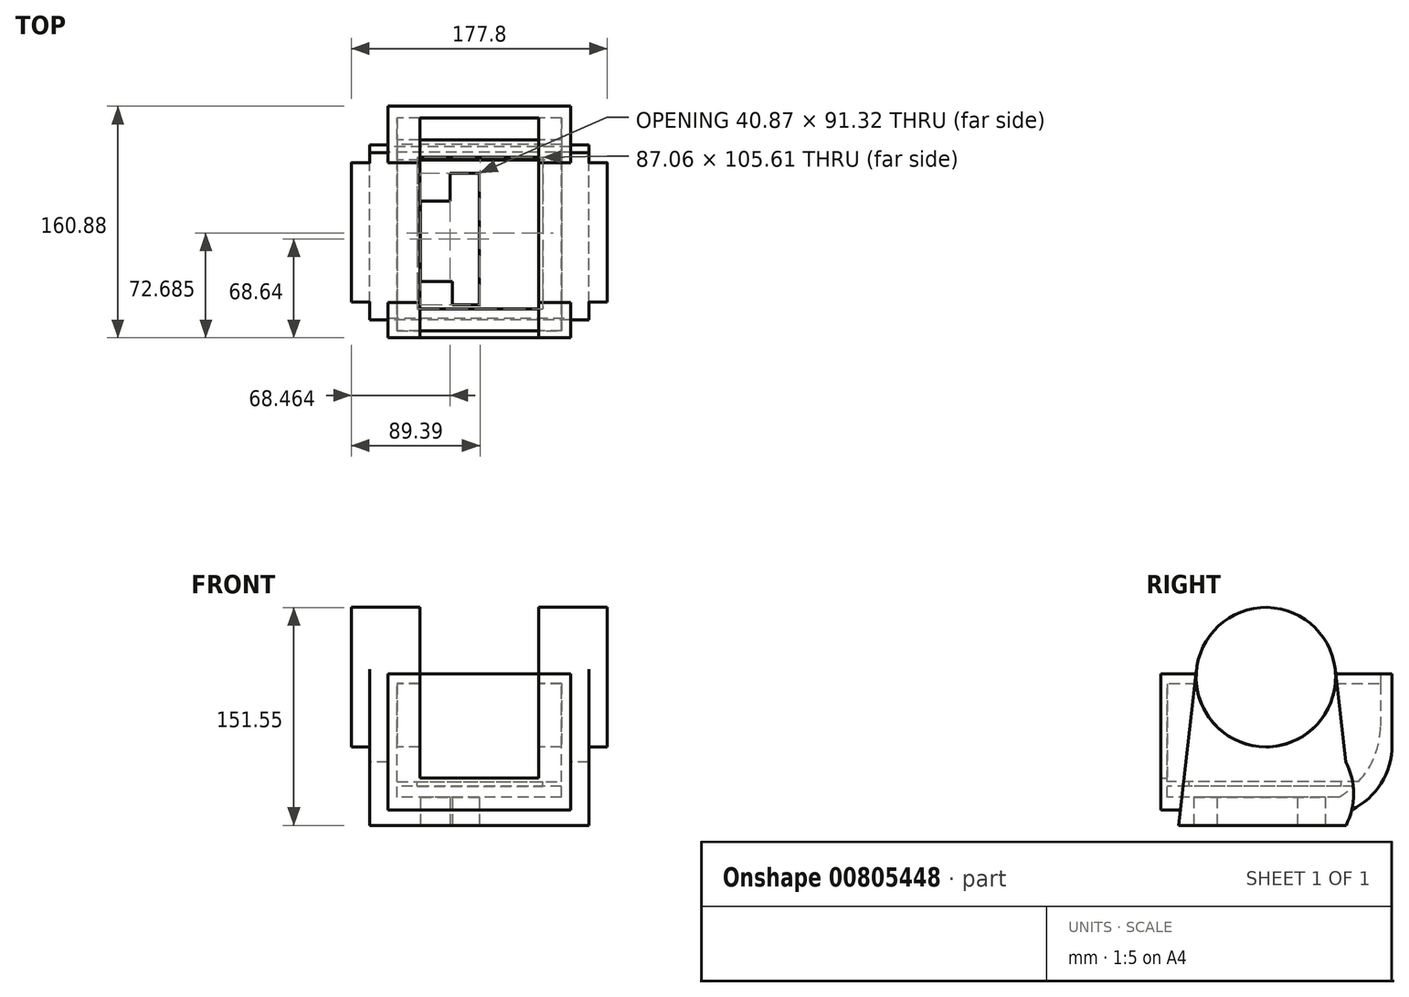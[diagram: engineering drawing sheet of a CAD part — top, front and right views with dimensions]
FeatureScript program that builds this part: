
annotation { "Feature Type Name" : "Feature", "Feature Type Description" : "" }
export const myFeature = defineFeature(function(context is Context, id is Id, definition is map)
    precondition{}
    {
        {
            var Q0;
            Q0=qCreatedBy(makeId("Right.planeOp"),FACE);
            var sketch = newSketch(context, id + "F0", { "sketchPlane" : qUnion([Q0])});
            skLineSegment(sketch, "E0", {"start": v(-58.2, 0) * mm, "end": v(58.24, 0) * mm});
            skArc(sketch, "E1", {"start": v(58.24, 0) * mm, "mid": v(63.47, 22.12) * mm, "end": v(58.05, 44.2) * mm});
            skLineSegment(sketch, "E2", {"start": v(58.05, 44.2) * mm, "end": v(50.61, 108.64) * mm});
            skArc(sketch, "E3", {"start": v(50.61, 108.64) * mm, "mid": v(2.47, 151.55) * mm, "end": v(-45.67, 108.64) * mm});
            skLineSegment(sketch, "E4", {"start": v(-45.67, 108.64) * mm, "end": v(-58.2, 0) * mm});
            skLineSegment(sketch, "E5", {"start": v(-45.67, 108.64) * mm, "end": v(50.61, 108.64) * mm, "construction": true});
            skSolve(sketch);
        }
        {
            var Q0;
            Q0 = qSketchRegion(id + "F0", true);
            extrude(context, id + "F1", {"entities" : qUnion([Q0]), "endBound" : BoundingType.SYMMETRIC, "depth" : 152.4 * mm, "offsetDistance" : 25.4 * mm});
        }
        {
            var Q0;
            Q0=qCreatedBy(makeId("Right.planeOp"),FACE);
            var sketch = newSketch(context, id + "F2", { "sketchPlane" : qUnion([Q0])});
            skCircle(sketch, "E6", {"center": v(2.47, 103.1) * mm, "radius": 48.46 * mm});
            skSolve(sketch);
        }
        {
            var Q0;
            Q0 = qSketchRegion(id + "F2", true);
            extrude(context, id + "F3", {"entities" : qUnion([Q0]), "operationType" : NewBodyOperationType.ADD, "endBound" : BoundingType.SYMMETRIC, "depth" : 177.8 * mm, "offsetDistance" : 25.4 * mm});
        }
        {
            var Q0;
            Q0=qCreatedBy(makeId("Right.planeOp"),FACE);
            var sketch = newSketch(context, id + "F4", { "sketchPlane" : qUnion([Q0])});
            skLineSegment(sketch, "E7", {"start": v(-70.63, 105.4) * mm, "end": v(90.25, 105.4) * mm});
            skLineSegment(sketch, "E8", {"start": v(90.25, 105.4) * mm, "end": v(90.25, 55.79) * mm});
            skArc(sketch, "E9", {"start": v(62.2, 10.85) * mm, "mid": v(82.66, 29.3) * mm, "end": v(90.25, 55.79) * mm});
            skLineSegment(sketch, "E10", {"start": v(-70.63, 105.4) * mm, "end": v(-70.63, 10.85) * mm});
            skLineSegment(sketch, "E11", {"start": v(-70.63, 10.85) * mm, "end": v(62.2, 10.85) * mm});
            skSolve(sketch);
        }
        {
            var Q0;
            Q0=makeQuery(id+"F4.imprint","IMPRINT",FACE,{"disambiguationData":[TD([[makeQuery(id+"F4.imprint","IMPRINT",EDGE,{"derivedFrom":sQuery(id+"F4.wireOp",EDGE,"E7")}),-1.0]])]});
            extrude(context, id + "F5", {"entities" : qUnion([Q0]), "operationType" : NewBodyOperationType.ADD, "endBound" : BoundingType.SYMMETRIC, "depth" : 127 * mm, "offsetDistance" : 25.4 * mm});
        }
        {
            var Q0;
            Q0=qCreatedBy(makeId("Right.planeOp"),FACE);
            var sketch = newSketch(context, id + "F6", { "sketchPlane" : qUnion([Q0])});
            skLineSegment(sketch, "E12", {"start": v(-101.25, 166.31) * mm, "end": v(82.15, 166.31) * mm});
            skLineSegment(sketch, "E13", {"start": v(82.15, 166.31) * mm, "end": v(82.15, 69.3) * mm});
            skLineSegment(sketch, "E14", {"start": v(-101.25, 166.31) * mm, "end": v(-101.25, 32.95) * mm});
            skLineSegment(sketch, "E15", {"start": v(-101.25, 32.95) * mm, "end": v(-65.98, 32.95) * mm});
            skLineSegment(sketch, "E16", {"start": v(-65.98, 32.95) * mm, "end": v(-65.98, 19.53) * mm});
            skLineSegment(sketch, "E17", {"start": v(-65.98, 19.53) * mm, "end": v(52.96, 19.53) * mm});
            skArc(sketch, "E18", {"start": v(52.96, 19.53) * mm, "mid": v(74.31, 40.44) * mm, "end": v(82.15, 69.3) * mm});
            skSolve(sketch);
        }
        {
            var Q0;
            Q0 = qSketchRegion(id + "F6", true);
            extrude(context, id + "F7", {"entities" : qUnion([Q0]), "operationType" : NewBodyOperationType.REMOVE, "endBound" : BoundingType.SYMMETRIC, "depth" : 82.55 * mm, "offsetDistance" : 25.4 * mm});
        }
        {
            var Q0;
            Q0=qCreatedBy(makeId("Right.planeOp"),FACE);
            var sketch = newSketch(context, id + "F8", { "sketchPlane" : qUnion([Q0])});
            skArc(sketch, "E19", {"start": v(-45.77, 98.44) * mm, "mid": v(2.54, 54.63) * mm, "end": v(50.72, 98.58) * mm});
            skLineSegment(sketch, "E20", {"start": v(82.15, 98.58) * mm, "end": v(50.72, 98.58) * mm});
            skLineSegment(sketch, "E21", {"start": v(82.15, 98.58) * mm, "end": v(82.15, 69.3) * mm});
            skArc(sketch, "E22", {"start": v(52.96, 19.53) * mm, "mid": v(74.31, 40.44) * mm, "end": v(82.15, 69.3) * mm});
            skLineSegment(sketch, "E23", {"start": v(52.96, 19.53) * mm, "end": v(-65.98, 19.53) * mm});
            skLineSegment(sketch, "E24", {"start": v(-65.98, 19.53) * mm, "end": v(-65.98, 98.44) * mm});
            skLineSegment(sketch, "E25", {"start": v(-65.98, 98.44) * mm, "end": v(-45.77, 98.44) * mm});
            skSolve(sketch);
        }
        {
            var Q0;
            Q0 = qSketchRegion(id + "F8", true);
            extrude(context, id + "F9", {"entities" : qUnion([Q0]), "operationType" : NewBodyOperationType.REMOVE, "endBound" : BoundingType.SYMMETRIC, "depth" : 114.3 * mm, "offsetDistance" : 25.4 * mm});
        }
        {
            var Q0;
            Q0=qCreatedBy(makeId("Top.planeOp"),FACE);
            cPlane(context, id + "F10", {"entities" : qUnion([Q0]), "cplaneType" : CPlaneType.OFFSET, "offset" : 30.48 * mm, "width" : 152.4 * mm, "height" : 152.4 * mm});
        }
        {
            var Q0;
            Q0=qCreatedBy(id+"F10.planeOp",FACE);
            var sketch = newSketch(context, id + "F11", { "sketchPlane" : qUnion([Q0])});
            skLineSegment(sketch, "E26.bottom", {"start": v(-61.46, 75.03) * mm, "end": v(61.16, 75.03) * mm});
            skLineSegment(sketch, "E26.top", {"start": v(-61.46, -68.19) * mm, "end": v(61.16, -68.19) * mm});
            skLineSegment(sketch, "E26.left", {"start": v(-61.46, 75.03) * mm, "end": v(-61.46, -68.19) * mm});
            skLineSegment(sketch, "E26.right", {"start": v(61.16, 75.03) * mm, "end": v(61.16, -68.19) * mm});
            skLineSegment(sketch, "E27.bottom", {"start": v(-43.04, 54.86) * mm, "end": v(44.02, 54.86) * mm});
            skLineSegment(sketch, "E27.top", {"start": v(-43.04, -50.75) * mm, "end": v(44.02, -50.75) * mm});
            skLineSegment(sketch, "E27.left", {"start": v(-43.04, 54.86) * mm, "end": v(-43.04, -50.75) * mm});
            skLineSegment(sketch, "E27.right", {"start": v(44.02, 54.86) * mm, "end": v(44.02, -50.75) * mm});
            skSolve(sketch);
        }
        {
            var Q0;
            Q0 = qSketchRegion(id + "F11", true);
            extrude(context, id + "F12", {"entities" : qUnion([Q0]), "operationType" : NewBodyOperationType.ADD, "oppositeDirection" : true, "depth" : 3.3 * mm, "offsetDistance" : 25.4 * mm});
        }
        {
            var Q0;
            Q0=qCreatedBy(makeId("Top.planeOp"),FACE);
            var sketch = newSketch(context, id + "F13", { "sketchPlane" : qUnion([Q0])});
            skLineSegment(sketch, "E28", {"start": v(-40.87, -31.54) * mm, "end": v(-40.87, 24.3) * mm});
            skLineSegment(sketch, "E29", {"start": v(-40.87, 24.3) * mm, "end": v(-20.34, 24.3) * mm});
            skLineSegment(sketch, "E30", {"start": v(-20.34, 24.3) * mm, "end": v(-20.34, 43.67) * mm});
            skLineSegment(sketch, "E31", {"start": v(-20.34, 43.67) * mm, "end": v(0, 43.67) * mm});
            skLineSegment(sketch, "E32", {"start": v(0, 43.67) * mm, "end": v(0, -47.65) * mm});
            skLineSegment(sketch, "E33", {"start": v(0, -47.65) * mm, "end": v(-18.8, -47.65) * mm});
            skLineSegment(sketch, "E34", {"start": v(-18.8, -47.65) * mm, "end": v(-18.8, -31.54) * mm});
            skLineSegment(sketch, "E35", {"start": v(-18.8, -31.54) * mm, "end": v(-40.87, -31.54) * mm});
            skSolve(sketch);
        }
        {
            var Q0;
            Q0 = qSketchRegion(id + "F13", true);
            extrude(context, id + "F14", {"entities" : qUnion([Q0]), "operationType" : NewBodyOperationType.REMOVE, "depth" : 25.4 * mm, "offsetDistance" : 25.4 * mm});
        }
    });
